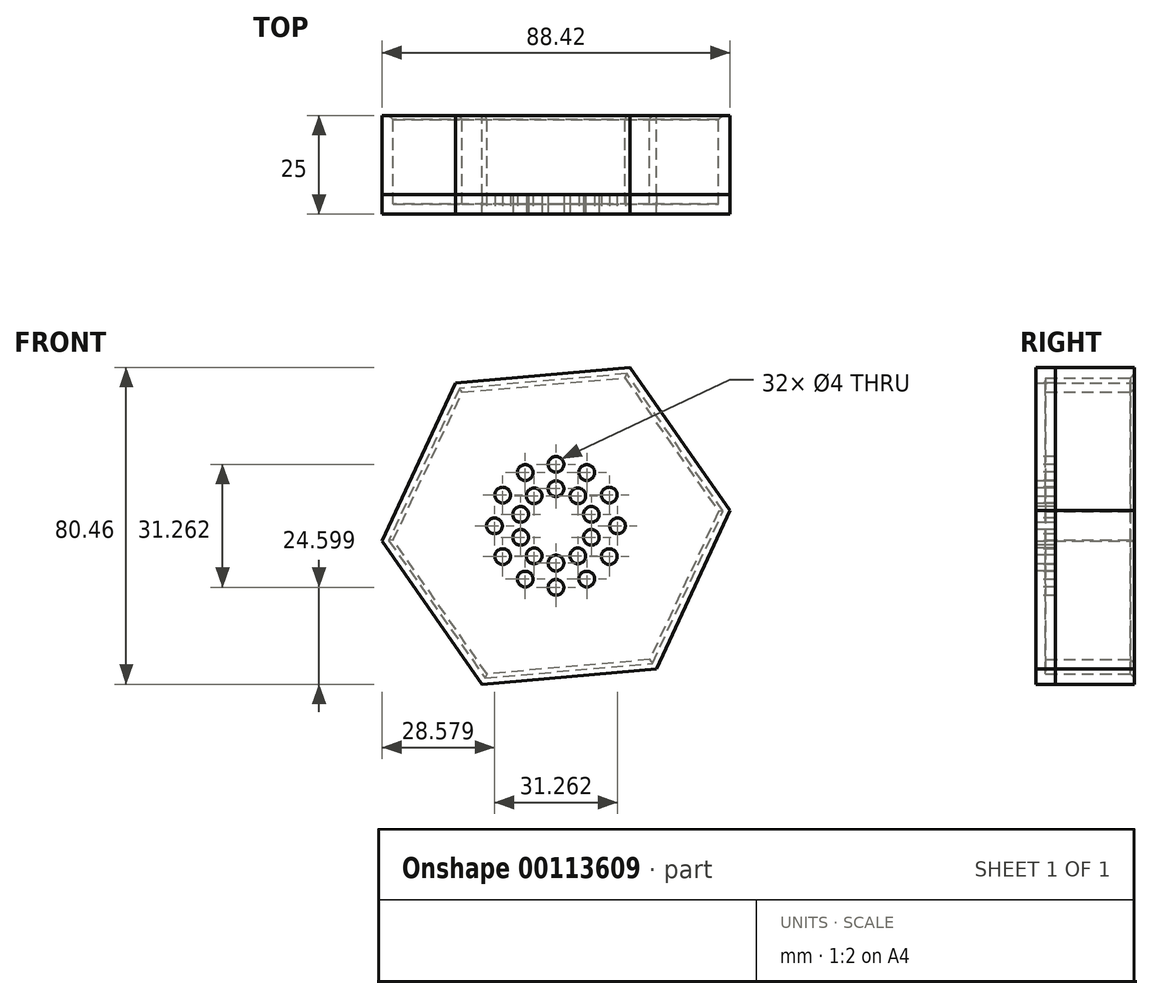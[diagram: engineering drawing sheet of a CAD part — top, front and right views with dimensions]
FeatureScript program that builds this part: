
annotation { "Feature Type Name" : "Feature", "Feature Type Description" : "" }
export const myFeature = defineFeature(function(context is Context, id is Id, definition is map)
    precondition{}
    {
        {
            var Q0;
            Q0=qCreatedBy(makeId("Front.planeOp"),FACE);
            var sketch = newSketch(context, id + "F0", { "sketchPlane" : qUnion([Q0])});
            skCircle(sketch, "E0.cCircle", {"center": v(0, 0) * mm, "radius": 38.44 * mm, "construction": true});
            skLineSegment(sketch, "E0.0", {"start": v(18.74, 40.23) * mm, "end": v(44.21, 3.88) * mm});
            skLineSegment(sketch, "E0.1", {"start": v(44.21, 3.88) * mm, "end": v(25.47, -36.35) * mm});
            skLineSegment(sketch, "E0.2", {"start": v(25.47, -36.35) * mm, "end": v(-18.74, -40.23) * mm});
            skLineSegment(sketch, "E0.3", {"start": v(-18.74, -40.23) * mm, "end": v(-44.21, -3.88) * mm});
            skLineSegment(sketch, "E0.4", {"start": v(-44.21, -3.88) * mm, "end": v(-25.47, 36.35) * mm});
            skLineSegment(sketch, "E0.5", {"start": v(-25.47, 36.35) * mm, "end": v(18.74, 40.23) * mm});
            skPoint(sketch, "E0.0.midPoint", {"position": v(31.48, 22.06) * mm});
            skSolve(sketch);
        }
        {
            var Q0;
            Q0=makeQuery(id+"F0.imprint","IMPRINT",FACE,{"disambiguationData":[TD([[makeQuery(id+"F0.imprint","IMPRINT",EDGE,{"derivedFrom":sQuery(id+"F0.wireOp",EDGE,"E0.0")}),-1.0]])]});
            extrude(context, id + "F1", {"entities" : qUnion([Q0]), "depth" : 25 * mm});
        }
        {
            var Q0;
            Q0=makeQuery(id+"F1.opExtrude","CAP_FACE",FACE,{"disambiguationData":[OSD([sQuery(id+"F0.wireOp",EDGE,"E0.0"),sQuery(id+"F0.wireOp",EDGE,"E0.1"),sQuery(id+"F0.wireOp",EDGE,"E0.2"),sQuery(id+"F0.wireOp",EDGE,"E0.3"),sQuery(id+"F0.wireOp",EDGE,"E0.4"),sQuery(id+"F0.wireOp",EDGE,"E0.5")])],"isStart":true});
            shell(context, id + "F2", {"entities" : qUnion([Q0]), "thickness" : 2.5 * mm});
        }
        {
            var Q0;
            Q0=makeQuery(id+"F1.opExtrude","CAP_FACE",FACE,{"disambiguationData":[OSD([sQuery(id+"F0.wireOp",EDGE,"E0.0"),sQuery(id+"F0.wireOp",EDGE,"E0.1"),sQuery(id+"F0.wireOp",EDGE,"E0.2"),sQuery(id+"F0.wireOp",EDGE,"E0.3"),sQuery(id+"F0.wireOp",EDGE,"E0.4"),sQuery(id+"F0.wireOp",EDGE,"E0.5")])],"isStart":false});
            var sketch = newSketch(context, id + "F3", { "sketchPlane" : qUnion([Q0])});
            skCircle(sketch, "E1", {"center": v(0, 15.63) * mm, "radius": 2 * mm});
            skCircle(sketch, "E2.1.0", {"center": v(7.82, 13.54) * mm, "radius": 2 * mm});
            skCircle(sketch, "E2.2.0", {"center": v(13.54, 7.82) * mm, "radius": 2 * mm});
            skCircle(sketch, "E2.3.0", {"center": v(15.63, 0) * mm, "radius": 2 * mm});
            skCircle(sketch, "E2.4.0", {"center": v(13.54, -7.82) * mm, "radius": 2 * mm});
            skCircle(sketch, "E2.5.0", {"center": v(7.82, -13.54) * mm, "radius": 2 * mm});
            skCircle(sketch, "E2.6.0", {"center": v(0, -15.63) * mm, "radius": 2 * mm});
            skCircle(sketch, "E2.7.0", {"center": v(-7.82, -13.54) * mm, "radius": 2 * mm});
            skCircle(sketch, "E2.8.0", {"center": v(-13.54, -7.82) * mm, "radius": 2 * mm});
            skCircle(sketch, "E2.9.0", {"center": v(-15.63, 0) * mm, "radius": 2 * mm});
            skCircle(sketch, "E2.10.0", {"center": v(-13.54, 7.82) * mm, "radius": 2 * mm});
            skCircle(sketch, "E2.11.0", {"center": v(-7.82, 13.54) * mm, "radius": 2 * mm});
            skPoint(sketch, "E2.center", {"position": v(0, 0) * mm});
            skLineSegment(sketch, "E2.anchor1", {"start": v(0, 0) * mm, "end": v(0, 15.63) * mm, "construction": true});
            skLineSegment(sketch, "E2.anchor2", {"start": v(0, 0) * mm, "end": v(-7.82, 13.54) * mm, "construction": true});
            skSolve(sketch);
        }
        {
            var Q0;
            Q0=makeQuery(id+"F3.imprint","IMPRINT",FACE,{"disambiguationData":[TD([[makeQuery(id+"F3.imprint","IMPRINT",EDGE,{"derivedFrom":sQuery(id+"F3.wireOp",EDGE,"E1")}),-1.0]])]});
            var Q1;
            Q1=sQuery(id+"F3.wireOp",EDGE,"E2.9.0");
            var Q2;
            Q2=sQuery(id+"F3.wireOp",EDGE,"E2.4.0");
            var Q3;
            Q3=sQuery(id+"F3.wireOp",EDGE,"E2.8.0");
            var Q4;
            Q4=sQuery(id+"F3.wireOp",EDGE,"E2.11.0");
            var Q5;
            Q5=sQuery(id+"F3.wireOp",EDGE,"E2.6.0");
            var Q6;
            Q6=sQuery(id+"F3.wireOp",EDGE,"E2.10.0");
            var Q7;
            Q7=sQuery(id+"F3.wireOp",EDGE,"E2.7.0");
            var Q8;
            Q8=sQuery(id+"F3.wireOp",EDGE,"E1");
            var Q9;
            Q9=sQuery(id+"F3.wireOp",EDGE,"E2.2.0");
            var Q10;
            Q10=sQuery(id+"F3.wireOp",EDGE,"E2.1.0");
            var Q11;
            Q11=sQuery(id+"F3.wireOp",EDGE,"E2.5.0");
            var Q12;
            Q12=sQuery(id+"F3.wireOp",EDGE,"E2.3.0");
            extrude(context, id + "F4", {"entities" : qUnion([Q0]), "surfaceEntities" : qUnion([Q1, Q2, Q3, Q4, Q5, Q6, Q7, Q8, Q9, Q10, Q11, Q12]), "oppositeDirection" : true, "depth" : 5 * mm});
        }
        {
            var Q0;
            {var subQ0=sQuery(id+"F0.wireOp",EDGE,"E0.3");Q0=makeQuery(id+"F2.opShell","OFFSET_EDGE",EDGE,{"disambiguationData":[OSD([subQ0]),TDD([makeQuery(id+"F1.opExtrude","CAP_EDGE",EDGE,{"disambiguationData":[OSD([subQ0])],"isStart":true})])]});}
            var Q1;
            {var subQ0=sQuery(id+"F0.wireOp",EDGE,"E0.4");Q1=makeQuery(id+"F2.opShell","OFFSET_EDGE",EDGE,{"disambiguationData":[OSD([subQ0]),TDD([makeQuery(id+"F1.opExtrude","CAP_EDGE",EDGE,{"disambiguationData":[OSD([subQ0])],"isStart":true})])]});}
            var Q2;
            {var subQ0=sQuery(id+"F0.wireOp",EDGE,"E0.2");Q2=makeQuery(id+"F2.opShell","OFFSET_EDGE",EDGE,{"disambiguationData":[OSD([subQ0]),TDD([makeQuery(id+"F1.opExtrude","CAP_EDGE",EDGE,{"disambiguationData":[OSD([subQ0])],"isStart":true})])]});}
            var Q3;
            {var subQ0=sQuery(id+"F0.wireOp",EDGE,"E0.5");Q3=makeQuery(id+"F2.opShell","OFFSET_EDGE",EDGE,{"disambiguationData":[OSD([subQ0]),TDD([makeQuery(id+"F1.opExtrude","CAP_EDGE",EDGE,{"disambiguationData":[OSD([subQ0])],"isStart":true})])]});}
            var Q4;
            {var subQ0=sQuery(id+"F0.wireOp",EDGE,"E0.0");Q4=makeQuery(id+"F2.opShell","OFFSET_EDGE",EDGE,{"disambiguationData":[OSD([subQ0]),TDD([makeQuery(id+"F1.opExtrude","CAP_EDGE",EDGE,{"disambiguationData":[OSD([subQ0])],"isStart":true})])]});}
            var Q5;
            {var subQ0=sQuery(id+"F0.wireOp",EDGE,"E0.1");Q5=makeQuery(id+"F2.opShell","OFFSET_EDGE",EDGE,{"disambiguationData":[OSD([subQ0]),TDD([makeQuery(id+"F1.opExtrude","CAP_EDGE",EDGE,{"disambiguationData":[OSD([subQ0])],"isStart":true})])]});}
            chamfer(context, id + "F5", {"entities" : qUnion([Q0, Q1, Q2, Q3, Q4, Q5]), "width" : 1 * mm, "tangentPropagation" : true});
        }
        {
            var Q0;
            Q0=makeQuery(id+"F1.opExtrude","CAP_FACE",FACE,{"disambiguationData":[OSD([sQuery(id+"F0.wireOp",EDGE,"E0.0"),sQuery(id+"F0.wireOp",EDGE,"E0.1"),sQuery(id+"F0.wireOp",EDGE,"E0.2"),sQuery(id+"F0.wireOp",EDGE,"E0.3"),sQuery(id+"F0.wireOp",EDGE,"E0.4"),sQuery(id+"F0.wireOp",EDGE,"E0.5")])],"isStart":false});
            var sketch = newSketch(context, id + "F6", { "sketchPlane" : qUnion([Q0])});
            skCircle(sketch, "E3", {"center": v(0, -9.44) * mm, "radius": 2 * mm});
            skCircle(sketch, "E4.1.0", {"center": v(5.55, -7.64) * mm, "radius": 2 * mm});
            skCircle(sketch, "E4.2.0", {"center": v(8.98, -2.92) * mm, "radius": 2 * mm});
            skCircle(sketch, "E4.3.0", {"center": v(8.98, 2.92) * mm, "radius": 2 * mm});
            skCircle(sketch, "E4.4.0", {"center": v(5.55, 7.64) * mm, "radius": 2 * mm});
            skCircle(sketch, "E4.5.0", {"center": v(0, 9.44) * mm, "radius": 2 * mm});
            skCircle(sketch, "E4.6.0", {"center": v(-5.55, 7.64) * mm, "radius": 2 * mm});
            skCircle(sketch, "E4.7.0", {"center": v(-8.98, 2.92) * mm, "radius": 2 * mm});
            skCircle(sketch, "E4.8.0", {"center": v(-8.98, -2.92) * mm, "radius": 2 * mm});
            skCircle(sketch, "E4.9.0", {"center": v(-5.55, -7.64) * mm, "radius": 2 * mm});
            skPoint(sketch, "E4.center", {"position": v(0, 0) * mm});
            skSolve(sketch);
        }
        {
            var Q0;
            Q0 = qSketchRegion(id + "F6", true);
            extrude(context, id + "F7", {"entities" : qUnion([Q0]), "operationType" : NewBodyOperationType.REMOVE, "oppositeDirection" : true, "depth" : 25 * mm});
        }
    });
